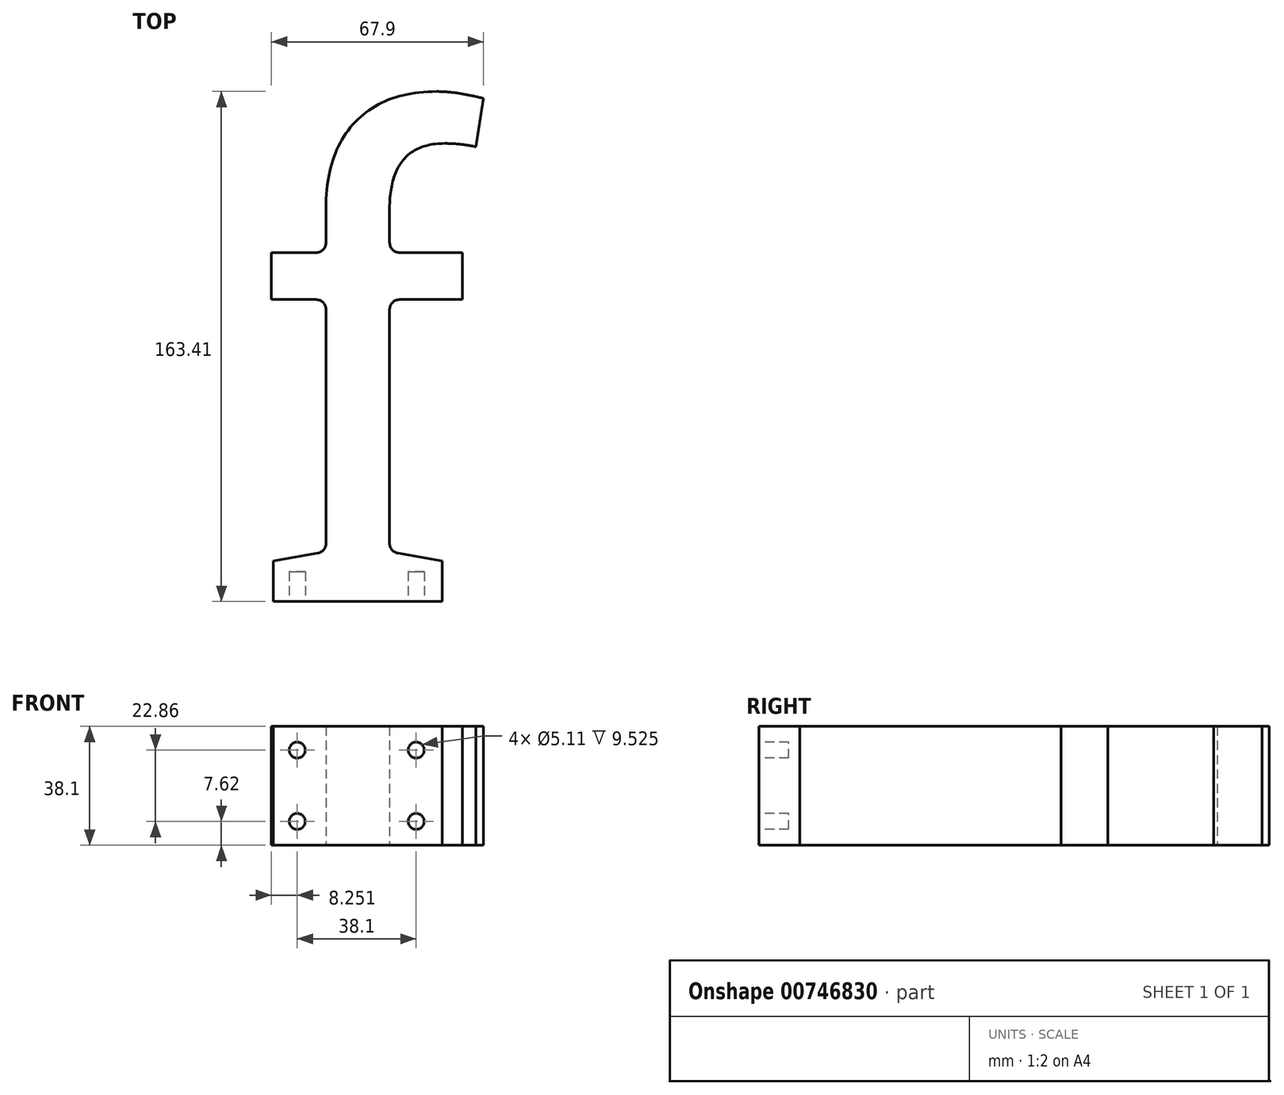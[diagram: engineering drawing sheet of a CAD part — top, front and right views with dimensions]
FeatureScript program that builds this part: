
annotation { "Feature Type Name" : "Feature", "Feature Type Description" : "" }
export const myFeature = defineFeature(function(context is Context, id is Id, definition is map)
    precondition{}
    {
        {
            var Q0;
            Q0=qCreatedBy(makeId("Top.planeOp"),FACE);
            var sketch = newSketch(context, id + "F0", { "sketchPlane" : qUnion([Q0])});
            skText(sketch, "E0", { "text": "f", "fontName": "RobotoSlab-Regular.ttf"});
            const initialGuessF0  = {"E0": [0, 0, 1, 0, 0.1524]};
            skSetInitialGuess(sketch, initialGuessF0);
            skSolve(sketch);
        }
        {
            var Q0;
            Q0=makeQuery(id+"F0.imprint","IMPRINT",FACE,{"disambiguationData":[TD([[makeQuery(id+"F0.imprint","IMPRINT",EDGE,{"derivedFrom":sQuery(id+"F0.wireOp",EDGE,"E0.sketch_text.stroke-0")}),-1.0]])]});
            extrude(context, id + "F1", {"entities" : qUnion([Q0]), "depth" : 38.1 * mm, "offsetDistance" : 25.4 * mm});
        }
        {
            var Q0;
            Q0=makeQuery(id+"F1.opExtrude","SWEPT_FACE",FACE,{"disambiguationData":[OSD([sQuery(id+"F0.wireOp",EDGE,"E0.sketch_text.stroke-19")])]});
            var sketch = newSketch(context, id + "F2", { "sketchPlane" : qUnion([Q0])});
            skCircle(sketch, "E1", {"center": v(15.5, 30.48) * mm, "radius": 2.55 * mm});
            skCircle(sketch, "E2", {"center": v(15.5, 7.62) * mm, "radius": 2.55 * mm});
            skCircle(sketch, "E3", {"center": v(53.6, 30.48) * mm, "radius": 2.55 * mm});
            skCircle(sketch, "E4", {"center": v(53.6, 7.62) * mm, "radius": 2.55 * mm});
            skSolve(sketch);
        }
        {
            var Q0;
            Q0=qSketchRegion(id+"F2",true);
            extrude(context, id + "F3", {"entities" : qUnion([Q0]), "operationType" : NewBodyOperationType.REMOVE, "oppositeDirection" : true, "depth" : 9.52 * mm, "offsetDistance" : 25.4 * mm});
        }
        {
            var Q0;
            Q0=makeQuery(id+"F1.opExtrude","SWEPT_EDGE",EDGE,{"disambiguationData":[OSD([sQuery(id+"F0.wireOp",EDGE,"E0.sketch_text.stroke-12"),sQuery(id+"F0.wireOp",EDGE,"E0.sketch_text.stroke-13")])]});
            var Q1;
            Q1=makeQuery(id+"F1.opExtrude","SWEPT_EDGE",EDGE,{"disambiguationData":[OSD([sQuery(id+"F0.wireOp",EDGE,"E0.sketch_text.stroke-1"),sQuery(id+"F0.wireOp",EDGE,"E0.sketch_text.stroke-2")])]});
            var Q2;
            Q2=makeQuery(id+"F1.opExtrude","SWEPT_EDGE",EDGE,{"disambiguationData":[OSD([sQuery(id+"F0.wireOp",EDGE,"E0.sketch_text.stroke-15"),sQuery(id+"F0.wireOp",EDGE,"E0.sketch_text.stroke-16")])]});
            var Q3;
            Q3=makeQuery(id+"F1.opExtrude","SWEPT_EDGE",EDGE,{"disambiguationData":[OSD([sQuery(id+"F0.wireOp",EDGE,"E0.sketch_text.stroke-22"),sQuery(id+"F0.wireOp",EDGE,"E0.sketch_text.stroke-23")])]});
            var Q4;
            Q4=makeQuery(id+"F1.opExtrude","SWEPT_EDGE",EDGE,{"disambiguationData":[OSD([sQuery(id+"F0.wireOp",EDGE,"E0.sketch_text.stroke-21"),sQuery(id+"F0.wireOp",EDGE,"E0.sketch_text.stroke-22")])]});
            var Q5;
            Q5=makeQuery(id+"F1.opExtrude","SWEPT_EDGE",EDGE,{"disambiguationData":[OSD([sQuery(id+"F0.wireOp",EDGE,"E0.sketch_text.stroke-16"),sQuery(id+"F0.wireOp",EDGE,"E0.sketch_text.stroke-17")])]});
            fillet(context, id + "F4", {"entities" : qUnion([Q0, Q1, Q2, Q3, Q4, Q5]), "radius" : 3.17 * mm, "tangentPropagation" : true, "allowEdgeOverflow" : false});
        }
    });
